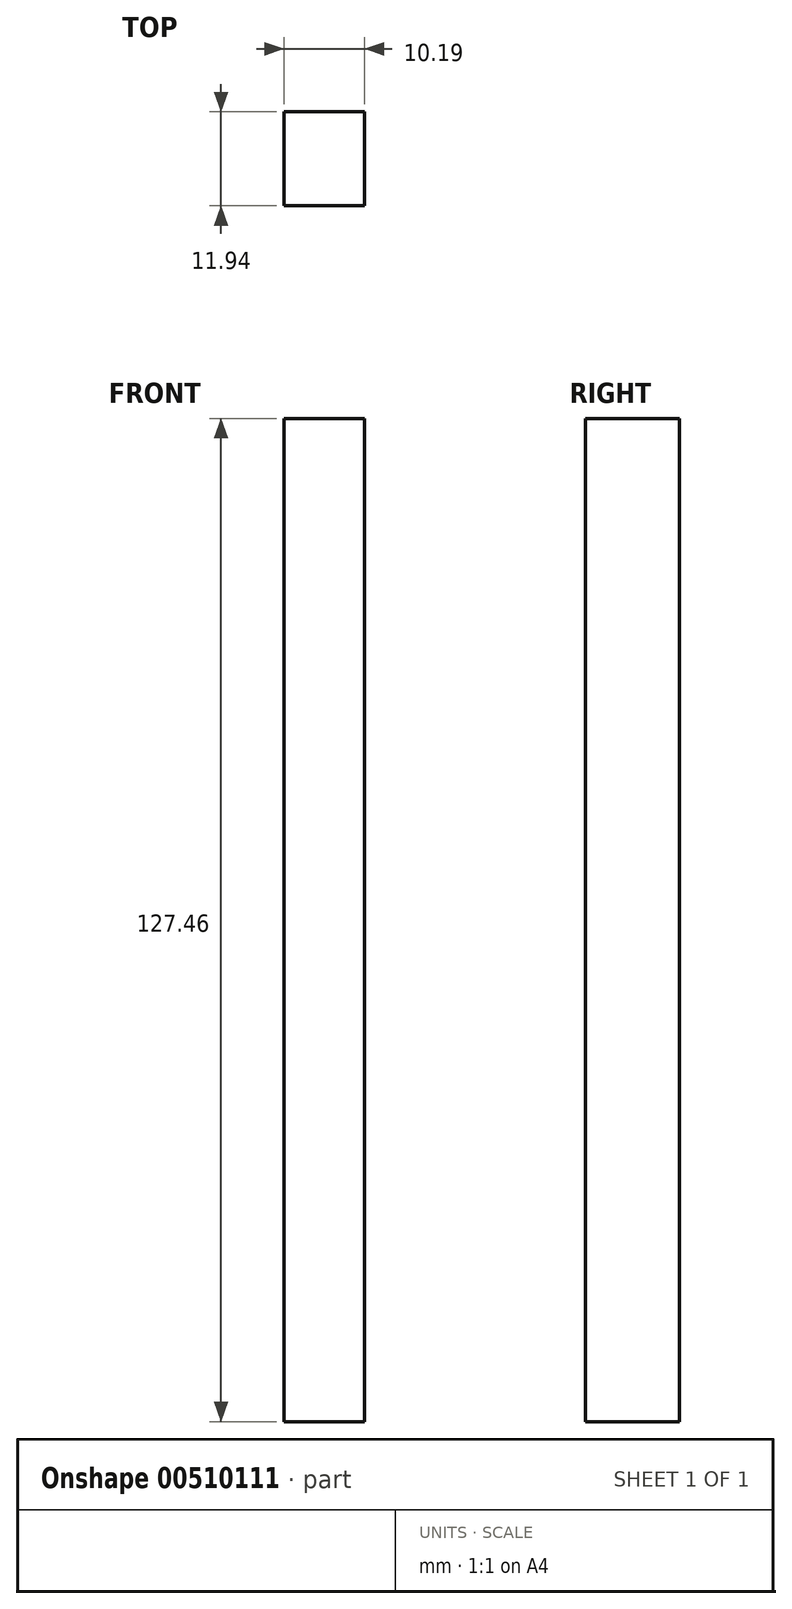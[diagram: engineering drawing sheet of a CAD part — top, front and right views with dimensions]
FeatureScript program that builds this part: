
annotation { "Feature Type Name" : "Feature", "Feature Type Description" : "" }
export const myFeature = defineFeature(function(context is Context, id is Id, definition is map)
    precondition{}
    {
        {
            var Q0;
            Q0=qCreatedBy(makeId("Front.planeOp"),FACE);
            var sketch = newSketch(context, id + "F0", { "sketchPlane" : qUnion([Q0])});
            skLineSegment(sketch, "E0", {"start": v(-40.23, -45.87) * mm, "end": v(-40.23, 81.59) * mm});
            skLineSegment(sketch, "E1", {"start": v(-40.23, 81.59) * mm, "end": v(-30.04, 81.59) * mm});
            skLineSegment(sketch, "E2", {"start": v(-30.04, 81.59) * mm, "end": v(-30.04, -45.87) * mm});
            skLineSegment(sketch, "E3", {"start": v(-30.04, -45.87) * mm, "end": v(-40.23, -45.87) * mm});
            skSolve(sketch);
        }
        {
            var Q0;
            Q0 = qSketchRegion(id + "F0", true);
            extrude(context, id + "F1", {"entities" : qUnion([Q0]), "depth" : 11.94 * mm});
        }
    });
